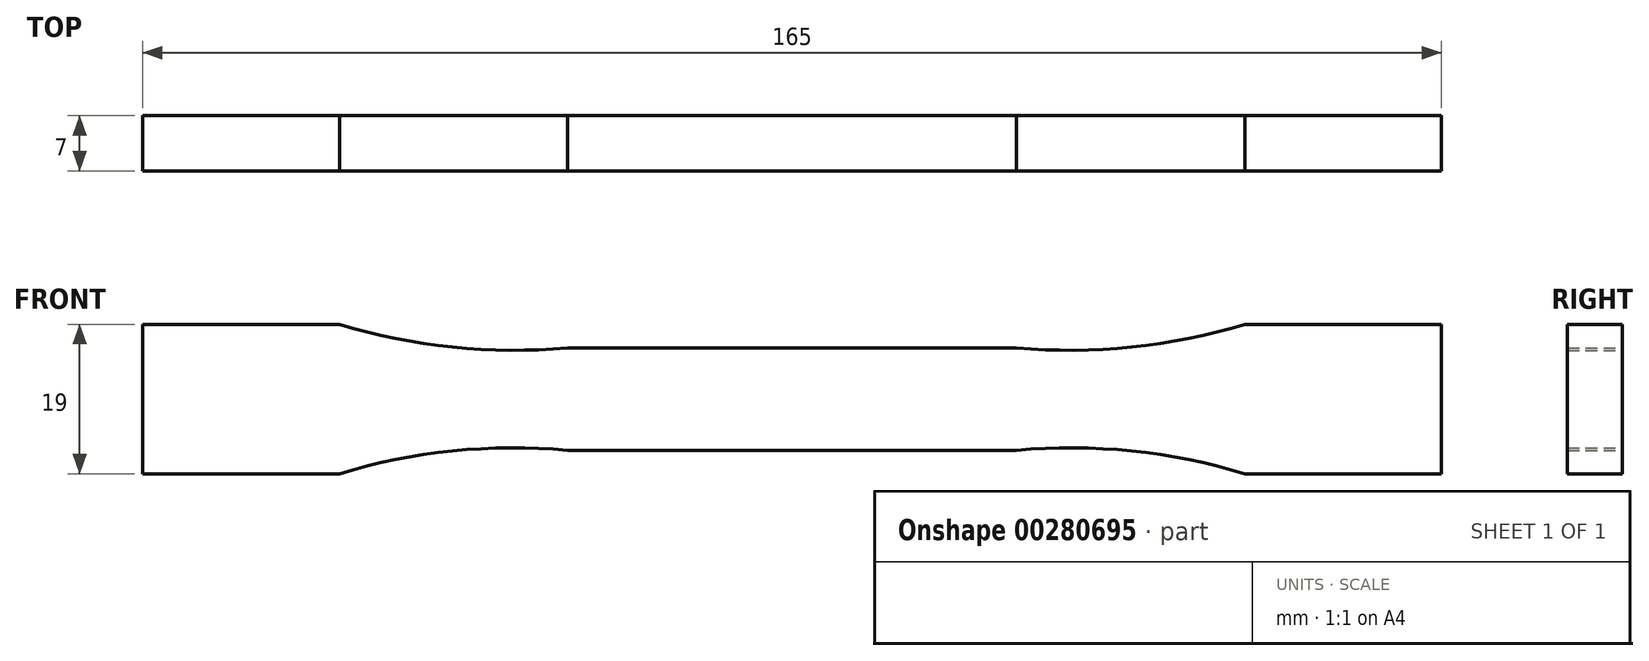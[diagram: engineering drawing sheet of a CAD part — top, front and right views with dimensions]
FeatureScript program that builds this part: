
annotation { "Feature Type Name" : "Feature", "Feature Type Description" : "" }
export const myFeature = defineFeature(function(context is Context, id is Id, definition is map)
    precondition{}
    {
        {
            var Q0;
            Q0=qCreatedBy(makeId("Front.planeOp"),FACE);
            var sketch = newSketch(context, id + "F0", { "sketchPlane" : qUnion([Q0])});
            skLineSegment(sketch, "E0", {"start": v(0, -6.5) * mm, "end": v(28.5, -6.5) * mm});
            skLineSegment(sketch, "E1", {"start": v(57.5, -9.5) * mm, "end": v(82.5, -9.5) * mm});
            skLineSegment(sketch, "E2.MirrorCS", {"start": v(57.5, 9.5) * mm, "end": v(82.5, 9.5) * mm});
            skLineSegment(sketch, "E3.MirrorCS", {"start": v(0, 6.5) * mm, "end": v(28.5, 6.5) * mm});
            skLineSegment(sketch, "E4.MirrorCS", {"start": v(0, 6.5) * mm, "end": v(-28.5, 6.5) * mm});
            skLineSegment(sketch, "E5.MirrorCS", {"start": v(-57.5, -9.5) * mm, "end": v(-82.5, -9.5) * mm});
            skLineSegment(sketch, "E6.MirrorCS", {"start": v(-57.5, 9.5) * mm, "end": v(-82.5, 9.5) * mm});
            skLineSegment(sketch, "E7.MirrorCS", {"start": v(0, -6.5) * mm, "end": v(-28.5, -6.5) * mm});
            skLineSegment(sketch, "E8", {"start": v(-82.5, 9.5) * mm, "end": v(-82.5, -9.5) * mm});
            skLineSegment(sketch, "E9", {"start": v(82.5, 9.5) * mm, "end": v(82.5, -9.5) * mm});
            skArc(sketch, "E10", {"start": v(-57.5, 9.5) * mm, "mid": v(-43.15, 6.6) * mm, "end": v(-28.5, 6.5) * mm});
            skArc(sketch, "E11", {"start": v(-28.5, -6.5) * mm, "mid": v(-43.15, -6.6) * mm, "end": v(-57.5, -9.5) * mm});
            skArc(sketch, "E12", {"start": v(28.5, 6.5) * mm, "mid": v(43.15, 6.6) * mm, "end": v(57.5, 9.5) * mm});
            skArc(sketch, "E13", {"start": v(57.5, -9.5) * mm, "mid": v(43.15, -6.6) * mm, "end": v(28.5, -6.5) * mm});
            skSolve(sketch);
        }
        {
            var Q0;
            Q0 = qSketchRegion(id + "F0", true);
            extrude(context, id + "F1", {"entities" : qUnion([Q0]), "endBound" : BoundingType.SYMMETRIC, "depth" : 7 * mm});
        }
    });
